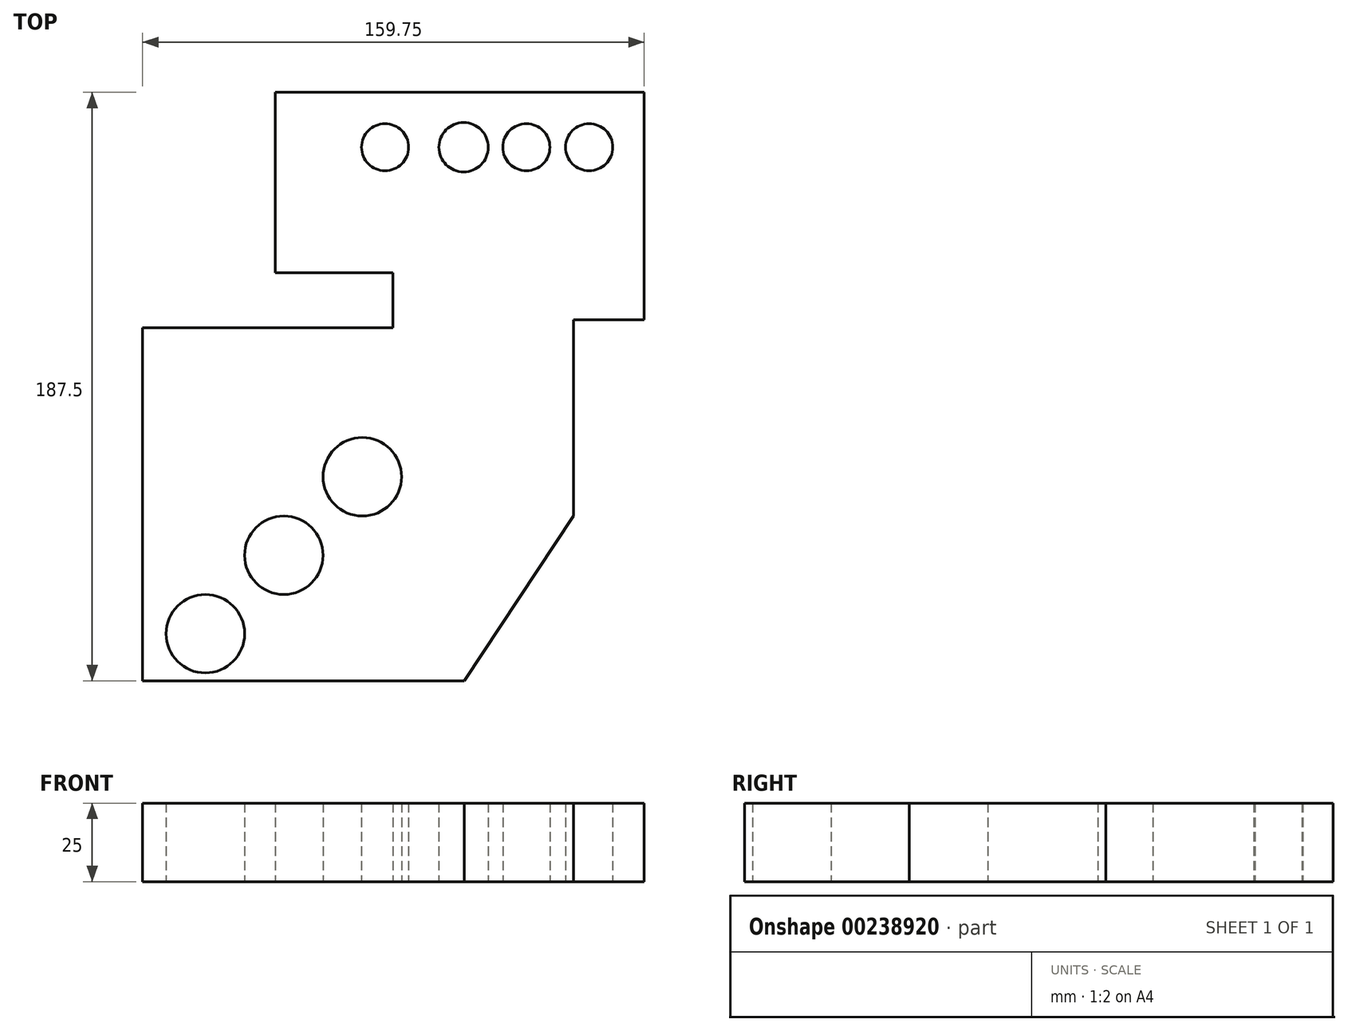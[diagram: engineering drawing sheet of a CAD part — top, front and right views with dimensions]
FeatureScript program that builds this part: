
annotation { "Feature Type Name" : "Feature", "Feature Type Description" : "" }
export const myFeature = defineFeature(function(context is Context, id is Id, definition is map)
    precondition{}
    {
        {
            var Q0;
            Q0=qCreatedBy(makeId("Top.planeOp"),FACE);
            var sketch = newSketch(context, id + "F0", { "sketchPlane" : qUnion([Q0])});
            skLineSegment(sketch, "E0", {"start": v(-102.25, -86.15) * mm, "end": v(-102.25, 26.35) * mm});
            skLineSegment(sketch, "E1", {"start": v(-102.25, 26.35) * mm, "end": v(-22.5, 26.35) * mm});
            skLineSegment(sketch, "E2", {"start": v(-22.5, 26.35) * mm, "end": v(-22.5, 43.85) * mm});
            skLineSegment(sketch, "E3", {"start": v(-22.5, 43.85) * mm, "end": v(-60, 43.85) * mm});
            skLineSegment(sketch, "E4", {"start": v(-60, 43.85) * mm, "end": v(-60, 101.35) * mm});
            skLineSegment(sketch, "E5", {"start": v(-60, 101.35) * mm, "end": v(57.5, 101.35) * mm});
            skLineSegment(sketch, "E6", {"start": v(57.5, 28.85) * mm, "end": v(35, 28.85) * mm});
            skLineSegment(sketch, "E7", {"start": v(35, 28.85) * mm, "end": v(35, -33.65) * mm});
            skLineSegment(sketch, "E8", {"start": v(35, -33.65) * mm, "end": v(0.25, -86.15) * mm});
            skLineSegment(sketch, "E9", {"start": v(57.5, 28.85) * mm, "end": v(57.5, 101.35) * mm});
            skCircle(sketch, "E10", {"center": v(-82.25, -71.15) * mm, "radius": 12.5 * mm});
            skLineSegment(sketch, "E11", {"start": v(0.25, -86.15) * mm, "end": v(-102.25, -86.15) * mm});
            skLineSegment(sketch, "E12", {"start": v(-102.25, -86.15) * mm, "end": v(-82.25, -86.15) * mm});
            skLineSegment(sketch, "E13", {"start": v(-82.25, -86.15) * mm, "end": v(-57.25, -86.15) * mm});
            skLineSegment(sketch, "E14", {"start": v(-57.25, -86.15) * mm, "end": v(-32.25, -86.15) * mm});
            skLineSegment(sketch, "E15", {"start": v(-102.25, -86.15) * mm, "end": v(-102.25, -46.15) * mm});
            skLineSegment(sketch, "E16", {"start": v(-102.25, -46.15) * mm, "end": v(-102.25, -21.15) * mm});
            skCircle(sketch, "E17", {"center": v(-57.25, -46.15) * mm, "radius": 12.5 * mm});
            skCircle(sketch, "E18", {"center": v(-32.25, -21.15) * mm, "radius": 12.5 * mm});
            skLineSegment(sketch, "E19", {"start": v(57.5, 101.35) * mm, "end": v(40, 101.35) * mm});
            skLineSegment(sketch, "E20", {"start": v(40, 101.35) * mm, "end": v(20, 101.35) * mm});
            skLineSegment(sketch, "E21", {"start": v(20, 101.35) * mm, "end": v(0, 101.35) * mm});
            skLineSegment(sketch, "E22", {"start": v(0, 101.35) * mm, "end": v(-25, 101.35) * mm});
            skLineSegment(sketch, "E23", {"start": v(57.5, 101.35) * mm, "end": v(57.5, 83.85) * mm});
            skLineSegment(sketch, "E24", {"start": v(40, 101.35) * mm, "end": v(40, 83.85) * mm});
            skCircle(sketch, "E25", {"center": v(40, 83.85) * mm, "radius": 7.5 * mm});
            skCircle(sketch, "E26", {"center": v(20, 83.85) * mm, "radius": 7.5 * mm});
            skCircle(sketch, "E27", {"center": v(0, 83.85) * mm, "radius": 7.86 * mm});
            skCircle(sketch, "E28", {"center": v(-25, 83.85) * mm, "radius": 7.5 * mm});
            skSolve(sketch);
        }
        {
            var Q0;
            Q0=makeQuery(id+"F0.imprint","IMPRINT",FACE,{"disambiguationData":[TD([[makeQuery(id+"F0.imprint","IMPRINT",EDGE,{"derivedFrom":sQuery(id+"F0.wireOp",EDGE,"E0")}),-1.0]])]});
            extrude(context, id + "F1", {"entities" : qUnion([Q0]), "depth" : 25 * mm});
        }
    });
